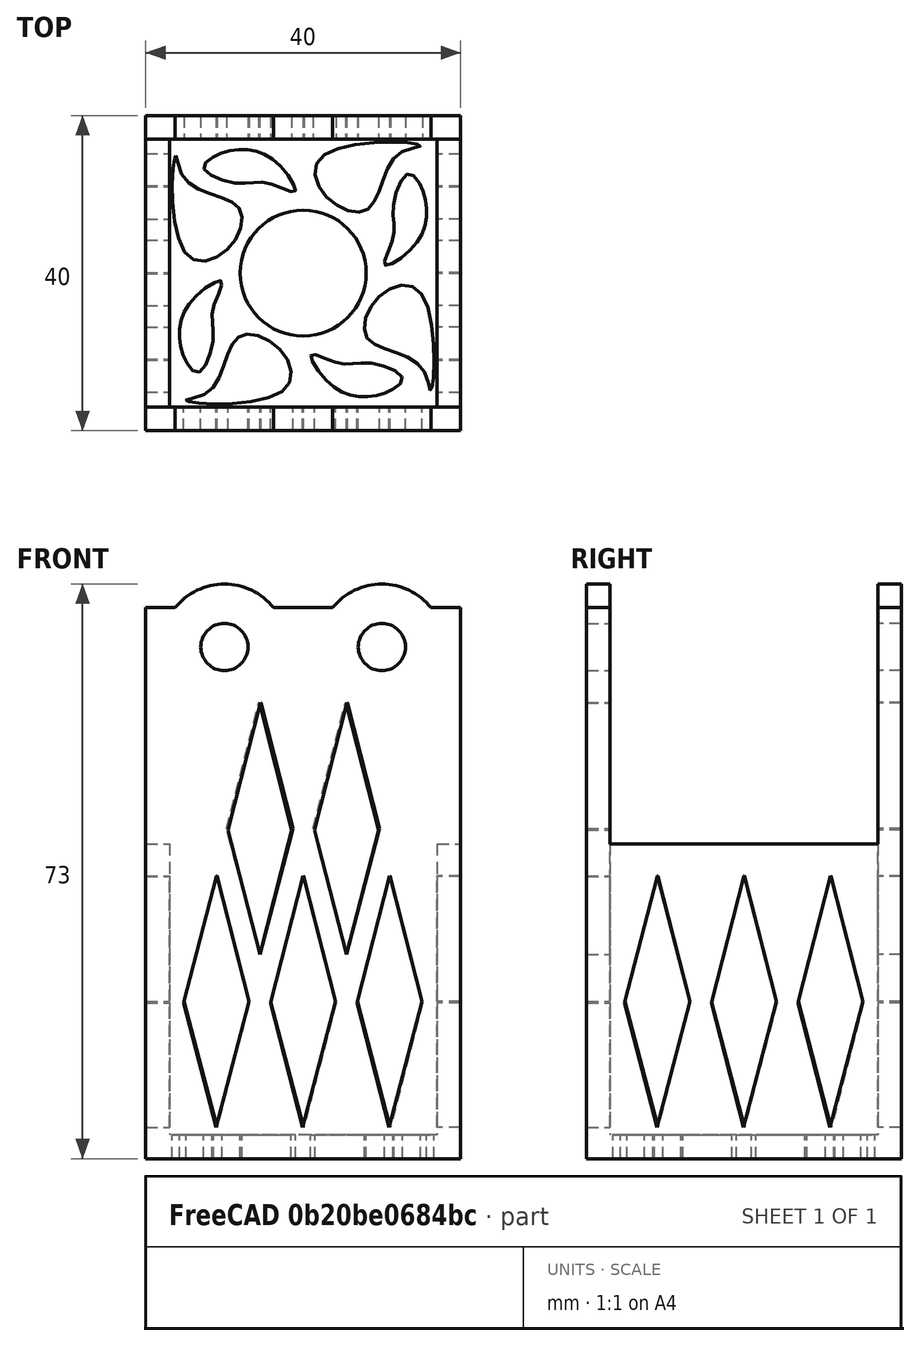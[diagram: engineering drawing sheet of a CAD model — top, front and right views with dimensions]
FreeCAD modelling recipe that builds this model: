
FCSTD DOCUMENT  (FreeCAD 0.16R6700 (Git))
Label: Laser mount v 1
License: All rights reserved
LicenseURL: http://en.wikipedia.org/wiki/All_rights_reserved
objects: Part::Cut×7, Part::Part2DObjectPython×6, Part::Extrusion×6, Part::Cylinder×5, Part::FeaturePython×5, Part::MultiFuse×5, Part::Box×2
note: 36 computed .brp shape members not serialized (recipe doc carries the construction recipe); baked Part::Feature solids carry a one-line shape summary decoded from their .brp

FEATURE [Part::Box] Box  label="Cube"
  Height = 40
  Length = 40
  Placement = pos=(-20,-20,0) rot=(0,0,1;0rad)
  Width = 40
FEATURE [Part::Part2DObjectPython] Rectangle  # Draft 2D object (typed FeaturePython)
  ChamferSize = 0
  Columns = 1
  FilletRadius = 0
  Height = 34
  Length = 34
  MakeFace = true
  Placement = pos=(17,17,40) rot=(0,0,1;3.14159rad)
  Rows = 1
FEATURE [Part::Extrusion] Extrude001
  Base = -> Rectangle
  Dir = (0,0,-37)
  Solid = false
FEATURE [Part::Cut] Cut
  Base = -> Box
  Tool = -> Extrude001
FEATURE [Part::Cylinder] Cylinder
  Angle = 360
  Height = 3
  Radius = 8
FEATURE [Part::Cut] Cut001  label="Chassis"
  Base = -> Cut
  Tool = -> Cylinder
FEATURE [Part::Part2DObjectPython] BSpline  label="Base vents 1"  # Draft 2D object (typed FeaturePython)
  Closed = true
  MakeFace = true
  Points = (5) [(-13.967,-15.8985,0),(-11.0044,-13.8617,0),(-8,-8,0),(-2.79563,-9.84993,0),(-2.11671,-14.5407,0)]
FEATURE [Part::FeaturePython] Array  label="Base Vents 1"  # Draft array (typed FeaturePython)
  Angle = 360
  ArrayType = 1
  Axis = (0,0,1)
  Base = -> BSpline
  Center = (0,0,0)
  Fuse = false
  IntervalAxis = (0,0,0)
  IntervalX = (1,0,0)
  IntervalY = (0,1,0)
  IntervalZ = (0,0,0)
  NumberPolar = 4
  NumberX = 2
  NumberY = 2
  NumberZ = 1
FEATURE [Part::Part2DObjectPython] BSpline002  # Draft 2D object (typed FeaturePython)
  Closed = true
  MakeFace = true
  Points = (6) [(-14.0287,-12.3805,-1.52656e-16),(-15.6335,-8.73896,0),(-13.2264,-2.56692,0),(-10.3872,-1.02391,0),(-11.4365,-4.48025,0),(-11.4365,-8.49208,0)]
FEATURE [Part::FeaturePython] Array001  label="Base vents 2"  # Draft array (typed FeaturePython)
  Angle = 360
  ArrayType = 1
  Axis = (0,0,1)
  Base = -> BSpline002
  Center = (0,0,0)
  Fuse = false
  IntervalAxis = (0,0,0)
  IntervalX = (1,0,0)
  IntervalY = (0,1,0)
  IntervalZ = (0,0,0)
  NumberPolar = 4
  NumberX = 2
  NumberY = 2
  NumberZ = 1
FEATURE [Part::Extrusion] Extrude
  Base = -> Array
  Dir = (0,0,3)
  Solid = false
FEATURE [Part::Extrusion] Extrude002
  Base = -> Array001
  Dir = (0,0,3)
  Solid = false
FEATURE [Part::MultiFuse] Fusion  label="Base vents"
  Shapes = -> [Extrude,Extrude002]
FEATURE [Part::Cut] Cut002  label="Chassis with base vents"
  Base = -> Cut001
  Tool = -> Fusion
FEATURE [Part::Cut] Cut003
  Base = -> Cut002
FEATURE [Part::Part2DObjectPython] DWire003  # Draft 2D object (typed FeaturePython)
  ChamferSize = 0
  Closed = true
  End = (0.0399391,-20,35.8827)
  FilletRadius = 0
  Length = 66.0594
  MakeFace = true
  Points = (5) [(-0.0217852,-20,35.9444),(-4.15705,-20,19.7737),(-0.0835034,-20,3.97325),(4.11348,-20,19.9588),(0.0399391,-20,35.8827)]
  Start = (-0.0217852,-20,35.9444)
  Subdivisions = 0
FEATURE [Part::Part2DObjectPython] DWire004  # Draft 2D object (typed FeaturePython)
  ChamferSize = 0
  Closed = true
  End = (-10.9601,-20,35.8827)
  FilletRadius = 0
  Length = 66.0594
  MakeFace = true
  Placement = pos=(-11,0,0) rot=(0,0,1;0rad)
  Points = (5) [(-0.0217852,-20,35.9444),(-4.15705,-20,19.7737),(-0.0835034,-20,3.97325),(4.11348,-20,19.9588),(0.0399391,-20,35.8827)]
  Start = (-11.0218,-20,35.9444)
  Subdivisions = 0
FEATURE [Part::Part2DObjectPython] DWire005  # Draft 2D object (typed FeaturePython)
  ChamferSize = 0
  Closed = true
  End = (11.0399,-20,35.8827)
  FilletRadius = 0
  Length = 66.0594
  MakeFace = true
  Placement = pos=(11,0,0) rot=(0,0,1;0rad)
  Points = (5) [(-0.0217852,-20,35.9444),(-4.15705,-20,19.7737),(-0.0835034,-20,3.97325),(4.11348,-20,19.9588),(0.0399391,-20,35.8827)]
  Start = (10.9782,-20,35.9444)
  Subdivisions = 0
FEATURE [Part::Extrusion] Extrude006
  Base = -> DWire003
  Dir = (0,3,0)
  Solid = false
FEATURE [Part::Extrusion] Extrude007
  Base = -> DWire004
  Dir = (0,3,0)
  Solid = false
FEATURE [Part::Extrusion] Extrude008
  Base = -> DWire005
  Dir = (0,3,0)
  Solid = false
FEATURE [Part::MultiFuse] Fusion002  label="Side Vents001"
  Shapes = -> [Extrude006,Extrude007,Extrude008]
FEATURE [Part::FeaturePython] Array002  label="Polar array of side vents"  # Draft array (typed FeaturePython)
  Angle = 360
  ArrayType = 1
  Axis = (0,0,1)
  Base = -> Fusion002
  Center = (0,0,0)
  Fuse = false
  IntervalAxis = (0,0,0)
  IntervalX = (1,0,0)
  IntervalY = (0,1,0)
  IntervalZ = (0,0,0)
  NumberPolar = 4
  NumberX = 2
  NumberY = 2
  NumberZ = 1
FEATURE [Part::Cut] Cut004  label="Chassis with all vents"
  Base = -> Cut003
  Tool = -> Array002
FEATURE [Part::Box] Box001  label="Cube001"
  Height = 30
  Length = 40
  Placement = pos=(-20,17,40) rot=(0,0,1;0rad)
  Width = 3
FEATURE [Part::Cylinder] Cylinder001
  Angle = 360
  Height = 3
  Placement = pos=(-10,20,65) rot=(1,0,0;1.5708rad)
  Radius = 3
FEATURE [Part::Cylinder] Cylinder002
  Angle = 360
  Height = 3
  Placement = pos=(-10,20,65) rot=(1,0,0;1.5708rad)
  Radius = 8
FEATURE [Part::Cylinder] Cylinder003
  Angle = 360
  Height = 3
  Placement = pos=(10,20,65) rot=(1,0,0;1.5708rad)
  Radius = 3
FEATURE [Part::Cylinder] Cylinder004
  Angle = 360
  Height = 3
  Placement = pos=(10,20,65) rot=(1,0,0;1.5708rad)
  Radius = 8
FEATURE [Part::MultiFuse] Fusion003  label="Screw point Left"
  Shapes = -> [Cylinder002,Box001,Cylinder004]
FEATURE [Part::MultiFuse] Fusion004  label="Screw holes"
  Shapes = -> [Cylinder003,Cylinder001]
FEATURE [Part::Cut] Cut005  label="Screw mounting point"
  Base = -> Fusion003
  Tool = -> Fusion004
FEATURE [Part::FeaturePython] Array003  label="Screw mounting points"  # Draft array (typed FeaturePython)
  Angle = 360
  ArrayType = 1
  Axis = (0,0,1)
  Base = -> Cut005
  Center = (0,0,0)
  Fuse = false
  IntervalAxis = (0,0,0)
  IntervalX = (1,0,0)
  IntervalY = (0,1,0)
  IntervalZ = (0,0,0)
  NumberPolar = 2
  NumberX = 2
  NumberY = 2
  NumberZ = 1
FEATURE [Part::MultiFuse] Fusion005  label="Mount without upper vents"
  Shapes = -> [Array003,Cut004]
FEATURE [Part::FeaturePython] Array004  label="Upper vents"  # Draft array (typed FeaturePython)
  Angle = 360
  ArrayType = 1
  Axis = (0,0,1)
  Center = (0,0,0)
  Fuse = false
  IntervalAxis = (0,0,0)
  IntervalX = (1,0,0)
  IntervalY = (0,1,0)
  IntervalZ = (0,0,0)
  NumberPolar = 2
  NumberX = 2
  NumberY = 2
  NumberZ = 1
FEATURE [Part::Cut] Cut006  label="Complete laser mount001"
  Base = -> Fusion005
  Tool = -> Array004
